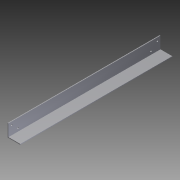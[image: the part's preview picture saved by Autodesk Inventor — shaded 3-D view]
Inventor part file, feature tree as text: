
AUTODESK INVENTOR PART (.ipt)
format: ipt  version: 2012 (Build 160160000, 160)  size: 91,648 bytes
history: native  units: in
note: dims shown in document units (in); Inventor stores cm internally (conversion verified against a paired STEP export)
features: extrude x2, sketch x2
ambient origin geometry x8: Origin, YZ Plane, XZ Plane, XY Plane, X Axis, Y Axis, Z Axis, Center Point
bodies: Solid1 (feature_tree)
feature tree (4):
  extrude  "Extrusion1"  Depth=1.0in
  extrude  "Extrusion4"  Depth=0.0625in
  sketch  "Sketch1"  dims[d0=1.0in d1=1.0in]
  sketch  "Sketch3"  dims[d2=0.0625in d3=0.0625in d4=12.0in d5=0.0in d19=0.25in d20=0.25in d21=0.3125in d22=0.75in d23=0.125in d24=1.0in d25=0.0in]
